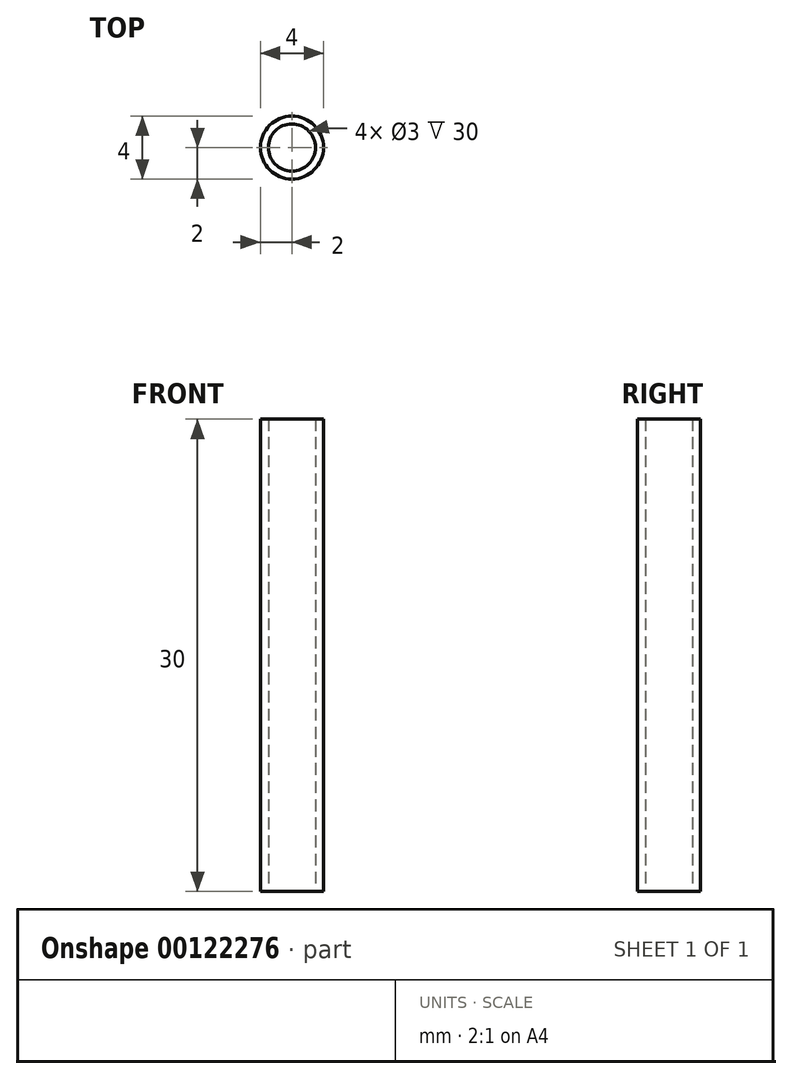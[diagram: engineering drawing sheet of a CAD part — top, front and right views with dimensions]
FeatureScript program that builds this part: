
annotation { "Feature Type Name" : "Feature", "Feature Type Description" : "" }
export const myFeature = defineFeature(function(context is Context, id is Id, definition is map)
    precondition{}
    {
        {
            var Q0;
            Q0=qCreatedBy(makeId("Top.planeOp"),FACE);
            var sketch = newSketch(context, id + "F0", { "sketchPlane" : qUnion([Q0])});
            skCircle(sketch, "E0", {"center": v(0, 0) * mm, "radius": 1.5 * mm});
            skCircle(sketch, "E1", {"center": v(0, 0) * mm, "radius": 2 * mm});
            skSolve(sketch);
        }
        {
            var Q0;
            Q0=makeQuery(id+"F0.imprint","IMPRINT",FACE,{"disambiguationData":[TD([[makeQuery(id+"F0.imprint","IMPRINT",EDGE,{"derivedFrom":sQuery(id+"F0.wireOp",EDGE,"E0")}),-1.0]])]});
            extrude(context, id + "F1", {"entities" : qUnion([Q0]), "depth" : 30 * mm});
        }
    });
